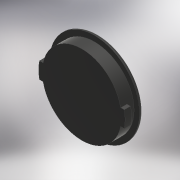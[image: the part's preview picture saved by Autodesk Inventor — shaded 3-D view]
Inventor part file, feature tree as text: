
AUTODESK INVENTOR PART (.ipt)
format: ipt  version: 2017 (Build 210142000, 142)  size: 680,448 bytes
history: native  units: mm
features: other x8, sketch x6, extrude x5, sheet_metal_op x1, fillet x1, projected_geometry x1
ambient origin geometry x8: Origin, YZ Plane, XZ Plane, XY Plane, X Axis, Y Axis, Z Axis, Center Point
bodies: Solide3 (feature_tree), Solide1 (feature_tree)
feature tree (22):
  other  "Boite_bas.ipt"
  other  "Plan de construction2"
  other  "Fond"
  sheet_metal_op  "Face"
  sketch  "Esquisse10"
  extrude  "Extrusion8"  Depth=10.0mm
  extrude  "Extrusion9"  Depth=2.5mm
  extrude  "Extrusion10"  Depth=4.0mm
  fillet  "Congé2"  Radius=0.5mm
  extrude  "Extrusion11"  Depth=7.0mm TaperAngle=0.0deg
  other  "Combiner2"
  other  "Plan de construction5"
  extrude  "Extrusion12"  Depth=2.0mm TaperAngle=0.0deg
  other  "Epaississement1"
  other  "Solide1::Boite_bas.ipt"
  other  "FonctionRepérage1"
  sketch  "Esquisse26"
  sketch  "Esquisse11"
  projected_geometry  "Boucle projetée5"
  sketch  "Esquisse12"
  sketch  "Esquisse13"
  sketch  "Esquisse15"
